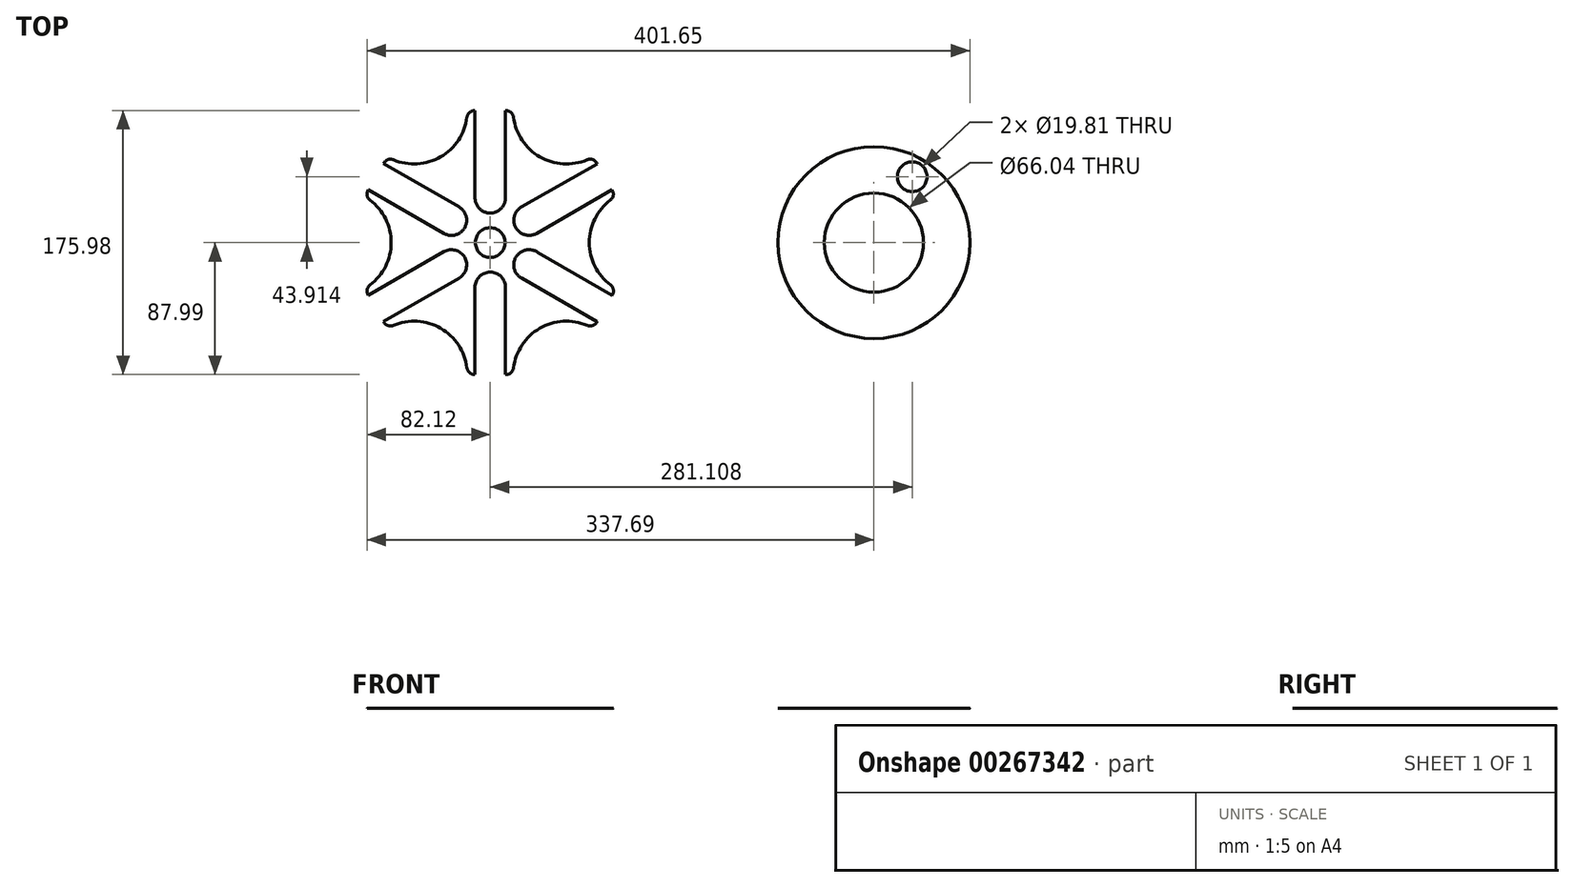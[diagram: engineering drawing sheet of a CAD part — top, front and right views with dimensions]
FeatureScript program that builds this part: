
annotation { "Feature Type Name" : "Feature", "Feature Type Description" : "" }
export const myFeature = defineFeature(function(context is Context, id is Id, definition is map)
    precondition{}
    {
        {
            var Q0;
            Q0=qCreatedBy(makeId("Top.planeOp"),FACE);
            var sketch = newSketch(context, id + "F0", { "sketchPlane" : qUnion([Q0])});
            skLineSegment(sketch, "E0", {"start": v(-17.88, 30.74) * mm, "end": v(-21.07, 36.23) * mm});
            skArc(sketch, "E1", {"start": v(-51.08, 88.15) * mm, "mid": v(-51.21, 88.23) * mm, "end": v(-51.35, 88.3) * mm});
            skLineSegment(sketch, "E2", {"start": v(-152.58, 87.67) * mm, "end": v(-152.68, 87.83) * mm});
            skArc(sketch, "E3.trimOffspring", {"start": v(-152.4, 87.99) * mm, "mid": v(-152.54, 87.9) * mm, "end": v(-152.68, 87.83) * mm});
            skArc(sketch, "E4", {"start": v(-17.78, 30.8) * mm, "mid": v(-35.56, 0) * mm, "end": v(-17.78, -30.8) * mm});
            skLineSegment(sketch, "E5", {"start": v(-17.78, -30.8) * mm, "end": v(-20.95, -36.3) * mm});
            skLineSegment(sketch, "E6", {"start": v(-86.36, -87.99) * mm, "end": v(-92.7, -87.99) * mm});
            skLineSegment(sketch, "E7", {"start": v(-170.18, -57.2) * mm, "end": v(-172.72, -52.8) * mm});
            skLineSegment(sketch, "E8.MirrorCS", {"start": v(-152.4, 87.99) * mm, "end": v(-152.58, 87.67) * mm});
            skLineSegment(sketch, "E9.MirrorCS", {"start": v(-86.36, 87.99) * mm, "end": v(-91.44, 87.99) * mm});
            skLineSegment(sketch, "E10.MirrorCS", {"start": v(-17.78, 30.8) * mm, "end": v(-20.95, 36.3) * mm});
            skArc(sketch, "E11", {"start": v(-33.02, -57.2) * mm, "mid": v(-68.58, -57.2) * mm, "end": v(-86.36, -87.99) * mm});
            skArc(sketch, "E12", {"start": v(-116.84, -87.99) * mm, "mid": v(-134.62, -57.2) * mm, "end": v(-170.18, -57.2) * mm});
            skArc(sketch, "E13", {"start": v(-185.42, -30.8) * mm, "mid": v(-167.64, 0) * mm, "end": v(-185.42, 30.8) * mm});
            skArc(sketch, "E14", {"start": v(-86.36, 87.99) * mm, "mid": v(-68.58, 57.2) * mm, "end": v(-33.02, 57.2) * mm});
            skArc(sketch, "E15", {"start": v(-170.18, 57.2) * mm, "mid": v(-134.62, 57.2) * mm, "end": v(-116.84, 87.99) * mm});
            skLineSegment(sketch, "E16.trimOffspring", {"start": v(-170.18, 57.2) * mm, "end": v(-173.35, 51.7) * mm});
            skLineSegment(sketch, "E17", {"start": v(-116.84, 87.99) * mm, "end": v(-111.76, 87.99) * mm});
            skLineSegment(sketch, "E18", {"start": v(-185.42, 30.8) * mm, "end": v(-182.25, 36.3) * mm});
            skLineSegment(sketch, "E19", {"start": v(-170.18, -57.2) * mm, "end": v(-173.35, -51.7) * mm});
            skLineSegment(sketch, "E20", {"start": v(-116.84, -87.99) * mm, "end": v(-110.5, -87.99) * mm});
            skLineSegment(sketch, "E21", {"start": v(-33.02, -57.2) * mm, "end": v(-29.85, -51.7) * mm});
            skLineSegment(sketch, "E22.trimOffspring", {"start": v(-182.25, 36.3) * mm, "end": v(-185.42, 30.8) * mm});
            skLineSegment(sketch, "E23.trimOffspring", {"start": v(-182.88, -35.2) * mm, "end": v(-185.42, -30.8) * mm});
            skLineSegment(sketch, "E24.trimOffspring", {"start": v(-29.84, 51.7) * mm, "end": v(-33.02, 57.2) * mm});
            skLineSegment(sketch, "E25.trimOffspring", {"start": v(-29.85, -51.7) * mm, "end": v(-33.02, -57.2) * mm});
            skLineSegment(sketch, "E26.trimOffspring", {"start": v(-110.5, -87.99) * mm, "end": v(-116.84, -87.99) * mm});
            skLineSegment(sketch, "E27", {"start": v(-131.93, 7.25) * mm, "end": v(-131.9, 7.22) * mm});
            skLineSegment(sketch, "E28", {"start": v(-80.13, 22.66) * mm, "end": v(-80.16, 22.64) * mm});
            skPoint(sketch, "E29.orphan", {"position": v(-68.58, 57.2) * mm});
            skPoint(sketch, "E30.orphan", {"position": v(-134.62, 57.2) * mm});
            skPoint(sketch, "E31.orphan", {"position": v(-134.62, -57.2) * mm});
            skPoint(sketch, "E32.orphan", {"position": v(-68.58, -57.2) * mm});
            skCircle(sketch, "E33.MirrorC", {"center": v(153.97, 0) * mm, "radius": 63.96 * mm});
            skCircle(sketch, "E34.MirrorC", {"center": v(153.97, 0) * mm, "radius": 33.02 * mm});
            skCircle(sketch, "E35.MirrorC", {"center": v(179.5, 43.91) * mm, "radius": 9.9 * mm});
            skPoint(sketch, "E36.orphan", {"position": v(-101.6, 79.1) * mm});
            skPoint(sketch, "E37.orphan", {"position": v(-101.6, -79.1) * mm});
            skPoint(sketch, "E38.orphan", {"position": v(-101.6, -39.55) * mm});
            skLineSegment(sketch, "E39", {"start": v(-71.33, 7.32) * mm, "end": v(-71.27, 7.25) * mm});
            skLineSegment(sketch, "E40.trimOffspring", {"start": v(-21.07, 36.23) * mm, "end": v(-20.95, 36.3) * mm});
            skCircle(sketch, "E41", {"center": v(-101.6, 0) * mm, "radius": 9.9 * mm});
            skLineSegment(sketch, "E42", {"start": v(-124.9, 19.32) * mm, "end": v(-124.98, 19.36) * mm});
            skLineSegment(sketch, "E43", {"start": v(-20.95, -36.3) * mm, "end": v(-22.86, -39.6) * mm});
            skLineSegment(sketch, "E44.trimOffspring", {"start": v(-27.94, -48.4) * mm, "end": v(-29.85, -51.7) * mm});
            skLineSegment(sketch, "E45.trimOffspring", {"start": v(-131.88, 7.25) * mm, "end": v(-131.9, 7.22) * mm});
            skPoint(sketch, "E46.trimOffspring.end.orphan", {"position": v(-80.16, 22.64) * mm});
            skPoint(sketch, "E47.start.orphan", {"position": v(-75.71, 14.95) * mm});
            skPoint(sketch, "E48.end.orphan", {"position": v(-92.7, 29.84) * mm});
            skPoint(sketch, "E49.start.orphan", {"position": v(-110.5, 29.85) * mm});
            skPoint(sketch, "E50.orphan", {"position": v(-168.39, 7.25) * mm});
            skLineSegment(sketch, "E51.trimOffspring", {"start": v(-131.88, 7.25) * mm, "end": v(-131.93, 7.25) * mm});
            skPoint(sketch, "E52.start.orphan", {"position": v(-94.85, 7.25) * mm});
            skPoint(sketch, "E53.trimOffspring.end.orphan", {"position": v(-92.7, -29.85) * mm});
            skArc(sketch, "E54", {"start": v(-111.76, 29.85) * mm, "mid": v(-101.6, 19.68) * mm, "end": v(-91.44, 29.84) * mm});
            skArc(sketch, "E55", {"start": v(-70.1, -6.48) * mm, "mid": v(-84.46, -9.68) * mm, "end": v(-80.57, -23.87) * mm});
            skArc(sketch, "E56", {"start": v(-91.44, -29.84) * mm, "mid": v(-101.6, -19.69) * mm, "end": v(-111.76, -29.85) * mm});
            skArc(sketch, "E57", {"start": v(-122.37, -23.72) * mm, "mid": v(-118.65, -9.84) * mm, "end": v(-132.53, -6.12) * mm});
            skArc(sketch, "E58", {"start": v(-132.53, 6.12) * mm, "mid": v(-118.63, 9.88) * mm, "end": v(-122.44, 23.76) * mm});
            skArc(sketch, "E59", {"start": v(-80.67, 23.81) * mm, "mid": v(-84.55, 9.93) * mm, "end": v(-70.63, 6.15) * mm});
            skLineSegment(sketch, "E60", {"start": v(-125.1, 19.16) * mm, "end": v(-124.98, 19.36) * mm});
            skLineSegment(sketch, "E61", {"start": v(-80.13, 22.66) * mm, "end": v(-80.17, 22.74) * mm});
            skLineSegment(sketch, "E62", {"start": v(-92.7, -29.85) * mm, "end": v(-83.38, -29.84) * mm});
            skLineSegment(sketch, "E63", {"start": v(-111.76, -29.85) * mm, "end": v(-119.88, -29.85) * mm});
            skLineSegment(sketch, "E64", {"start": v(-132.53, -6.12) * mm, "end": v(-184.78, -36.3) * mm});
            skLineSegment(sketch, "E65", {"start": v(-122.37, -23.72) * mm, "end": v(-175.15, -54.2) * mm});
            skLineSegment(sketch, "E66", {"start": v(-132.53, 6.12) * mm, "end": v(-182.88, 35.2) * mm});
            skLineSegment(sketch, "E67", {"start": v(-122.44, 23.76) * mm, "end": v(-173.35, 53.16) * mm});
            skLineSegment(sketch, "E68", {"start": v(-111.76, 29.85) * mm, "end": v(-111.76, 87.99) * mm});
            skLineSegment(sketch, "E69", {"start": v(-91.44, 29.84) * mm, "end": v(-91.44, 87.99) * mm});
            skLineSegment(sketch, "E70", {"start": v(-71.27, -5.8) * mm, "end": v(-7.8, -42.45) * mm});
            skLineSegment(sketch, "E71", {"start": v(-80.57, -23.87) * mm, "end": v(-13.2, -62.76) * mm});
            skLineSegment(sketch, "E72", {"start": v(-80.75, 23.77) * mm, "end": v(-80.67, 23.81) * mm});
            skLineSegment(sketch, "E73", {"start": v(-70.63, 6.15) * mm, "end": v(-12.6, 39.65) * mm});
            skLineSegment(sketch, "E74", {"start": v(-80.75, 23.77) * mm, "end": v(-18.8, 58.78) * mm});
            skLineSegment(sketch, "E75", {"start": v(-111.76, -29.85) * mm, "end": v(-111.76, -93.35) * mm});
            skLineSegment(sketch, "E76", {"start": v(-91.44, -29.84) * mm, "end": v(-91.44, -93.34) * mm});
            skPoint(sketch, "E77.trimOffspring.end.orphan", {"position": v(-92.7, 87.99) * mm});
            skPoint(sketch, "E78.orphan", {"position": v(-182.25, -36.3) * mm});
            skPoint(sketch, "E79.trimOffspring.end.orphan", {"position": v(-13.2, -56.9) * mm});
            skLineSegment(sketch, "E80.trimOffspring", {"start": v(-22.86, -39.6) * mm, "end": v(-15.66, -43.75) * mm});
            skPoint(sketch, "E81.start.orphan", {"position": v(-96.52, -29.85) * mm});
            skLineSegment(sketch, "E82.trimOffspring", {"start": v(-70.63, 6.15) * mm, "end": v(-67.08, 0) * mm});
            skLineSegment(sketch, "E83.trimOffspring", {"start": v(-80.75, 23.77) * mm, "end": v(-83.93, 29.4) * mm});
            skPoint(sketch, "E84.orphan", {"position": v(-96.52, 29.84) * mm});
            skPoint(sketch, "E85.end.orphan", {"position": v(-119.88, -28.03) * mm});
            skCircle(sketch, "E86", {"center": v(153.97, 0) * mm, "radius": 9.9 * mm});
            skSolve(sketch);
        }
        {
            var Q0;
            {var subQ4=sQuery(id+"F0.wireOp",EDGE,"E5");Q0=makeQuery(id+"F0.imprint","IMPRINT",FACE,{"disambiguationData":[TD([[makeQuery(id+"F0.imprint","IMPRINT",EDGE,{"derivedFrom":subQ4}),-1.0]])]});}
            var Q1;
            {var subQ0=sQuery(id+"F0.wireOp",EDGE,"E22.trimOffspring");Q1=makeQuery(id+"F0.imprint","IMPRINT",FACE,{"disambiguationData":[TD([[makeQuery(id+"F0.imprint","IMPRINT",EDGE,{"derivedFrom":subQ0}),1.0]])]});}
            var Q2;
            Q2=makeQuery(id+"F0.imprint","IMPRINT",FACE,{"disambiguationData":[TD([[makeQuery(id+"F0.imprint","IMPRINT",EDGE,{"derivedFrom":sQuery(id+"F0.wireOp",EDGE,"uSZaNnna-1jwC-4t9j-SezL-AJG7YBYIZrXv")}),-1.0]])]});
            var Q3;
            Q3=makeQuery(id+"F0.imprint","IMPRINT",FACE,{"disambiguationData":[TD([[makeQuery(id+"F0.imprint","IMPRINT",EDGE,{"derivedFrom":sQuery(id+"F0.wireOp",EDGE,"D1ePEbcy-xajl-UQ1t-o9PS-B0dAxn1GL7n1")}),1.0]])]});
            var Q4;
            Q4=makeQuery(id+"F0.imprint","IMPRINT",FACE,{"disambiguationData":[TD([[makeQuery(id+"F0.imprint","IMPRINT",EDGE,{"derivedFrom":sQuery(id+"F0.wireOp",EDGE,"ikVYGcS1-sRuT-H6B9-o1VI-YZQh97ZToIua")}),1.0]])]});
            var Q5;
            {var subQ6=sQuery(id+"F0.wireOp",EDGE,"dRBBgPbQ-JmLF-MllI-72Dp-3rJgf66h9gDL");Q5=makeQuery(id+"F0.imprint","IMPRINT",FACE,{"disambiguationData":[TD([[makeQuery(id+"F0.imprint","IMPRINT",EDGE,{"derivedFrom":subQ6}),-1.0]])]});}
            var Q6;
            {var subQ0=sQuery(id+"F0.wireOp",EDGE,"KPSCcwpI-83Hp-GgRb-4KHc-9A43FENirF3n");Q6=makeQuery(id+"F0.imprint","IMPRINT",FACE,{"disambiguationData":[TD([[makeQuery(id+"F0.imprint","IMPRINT",EDGE,{"derivedFrom":subQ0}),-1.0]])]});}
            var Q7;
            Q7=makeQuery(id+"F0.imprint","IMPRINT",FACE,{"disambiguationData":[TD([[makeQuery(id+"F0.imprint","IMPRINT",EDGE,{"derivedFrom":sQuery(id+"F0.wireOp",EDGE,"4uL0ZJAi-WeLn-BYnS-dUuS-PUcKbwxaNKFB")}),-1.0]])]});
            var Q8;
            Q8=makeQuery(id+"F0.imprint","IMPRINT",FACE,{"disambiguationData":[TD([[makeQuery(id+"F0.imprint","IMPRINT",EDGE,{"derivedFrom":sQuery(id+"F0.wireOp",EDGE,"Ppr8QDiS-9UEB-n1fa-jZbn-iAMovaq8OuiE")}),1.0]])]});
            var Q9;
            {var subQ4=sQuery(id+"F0.wireOp",EDGE,"8d62YASr-I1gK-Lq7n-FRaW-UgMCD8gDFPTT");Q9=makeQuery(id+"F0.imprint","IMPRINT",FACE,{"disambiguationData":[TD([[makeQuery(id+"F0.imprint","IMPRINT",EDGE,{"derivedFrom":subQ4}),1.0]])]});}
            var Q10;
            {var subQ1=sQuery(id+"F0.wireOp",EDGE,"E40.trimOffspring");var subQ7=makeQuery(id+"F0.imprint","INTERSECT",VERTEX,{"derivedFrom":[sQuery(id+"F0.wireOp",EDGE,"E0"),subQ1]});Q10=makeQuery(id+"F0.imprint","IMPRINT",FACE,{"disambiguationData":[TD([[makeQuery(id+"F0.imprint","IMPRINT",EDGE,{"disambiguationData":[TD([[subQ7,1.0]])],"derivedFrom":subQ1}),1.0]])]});}
            var Q11;
            Q11=makeQuery(id+"F0.imprint","IMPRINT",FACE,{"disambiguationData":[TD([[makeQuery(id+"F0.imprint","IMPRINT",EDGE,{"derivedFrom":sQuery(id+"F0.wireOp",EDGE,"E48")}),-1.0]])]});
            var Q12;
            Q12=makeQuery(id+"F0.imprint","IMPRINT",FACE,{"disambiguationData":[TD([[makeQuery(id+"F0.imprint","IMPRINT",EDGE,{"derivedFrom":sQuery(id+"F0.wireOp",EDGE,"wmZiJQRu-9ril-CLY3-VCLZ-qn6qzMTUEO2v")}),1.0]])]});
            var Q13;
            Q13=makeQuery(id+"F0.imprint","IMPRINT",FACE,{"disambiguationData":[TD([[makeQuery(id+"F0.imprint","IMPRINT",EDGE,{"derivedFrom":sQuery(id+"F0.wireOp",EDGE,"BJWzxmc5-WlMr-A5qr-5WOj-xHkCWyfmV3LD")}),-1.0]])]});
            var Q14;
            Q14=makeQuery(id+"F0.imprint","IMPRINT",FACE,{"disambiguationData":[TD([[makeQuery(id+"F0.imprint","IMPRINT",EDGE,{"derivedFrom":sQuery(id+"F0.wireOp",EDGE,"CQ3IfXNZ-0Cpx-K8aI-YxXh-zfcO3uTLte8J")}),1.0]])]});
            var Q15;
            Q15=makeQuery(id+"F0.imprint","IMPRINT",FACE,{"disambiguationData":[TD([[makeQuery(id+"F0.imprint","IMPRINT",EDGE,{"derivedFrom":sQuery(id+"F0.wireOp",EDGE,"WXQhSTUE-mwQW-dd3I-SJBa-6qlZWPCet8Dx")}),-1.0]])]});
            var Q16;
            Q16=makeQuery(id+"F0.imprint","IMPRINT",FACE,{"disambiguationData":[TD([[makeQuery(id+"F0.imprint","IMPRINT",EDGE,{"derivedFrom":sQuery(id+"F0.wireOp",EDGE,"TLkUIHZT-hsmt-kgMV-qJ7m-XfVgcyBmOZD1")}),1.0]])]});
            extrude(context, id + "F1", {"entities" : qUnion([Q0, Q1, Q2, Q3, Q4, Q5, Q6, Q7, Q8, Q9, Q10, Q11, Q12, Q13, Q14, Q15, Q16]), "depth" : 1 / 203.2 * mm});
        }
        {
            var Q0;
            Q0=makeQuery(id+"F1.opExtrude","SWEPT_EDGE",EDGE,{"disambiguationData":[OSD([sQuery(id+"F0.wireOp",EDGE,"E0"),sQuery(id+"F0.wireOp",EDGE,"E4")])]});
            var Q1;
            Q1=makeQuery(id+"F1.opExtrude","SWEPT_EDGE",EDGE,{"disambiguationData":[OSD([sQuery(id+"F0.wireOp",EDGE,"E4"),sQuery(id+"F0.wireOp",EDGE,"E5")])]});
            var Q2;
            Q2=makeQuery(id+"F1.opExtrude","SWEPT_EDGE",EDGE,{"disambiguationData":[OSD([sQuery(id+"F0.wireOp",EDGE,"E11"),sQuery(id+"F0.wireOp",EDGE,"E25.trimOffspring")])]});
            var Q3;
            Q3=makeQuery(id+"F1.opExtrude","SWEPT_EDGE",EDGE,{"disambiguationData":[OSD([sQuery(id+"F0.wireOp",EDGE,"E6"),sQuery(id+"F0.wireOp",EDGE,"E11")])]});
            var Q4;
            Q4=makeQuery(id+"F1.opExtrude","SWEPT_EDGE",EDGE,{"disambiguationData":[OSD([sQuery(id+"F0.wireOp",EDGE,"E12"),sQuery(id+"F0.wireOp",EDGE,"E26.trimOffspring")])]});
            var Q5;
            Q5=makeQuery(id+"F1.opExtrude","SWEPT_EDGE",EDGE,{"disambiguationData":[OSD([sQuery(id+"F0.wireOp",EDGE,"E12"),sQuery(id+"F0.wireOp",EDGE,"E19")])]});
            var Q6;
            Q6=makeQuery(id+"F1.opExtrude","SWEPT_EDGE",EDGE,{"disambiguationData":[OSD([sQuery(id+"F0.wireOp",EDGE,"E13"),sQuery(id+"F0.wireOp",EDGE,"E23.trimOffspring")])]});
            var Q7;
            Q7=makeQuery(id+"F1.opExtrude","SWEPT_EDGE",EDGE,{"disambiguationData":[OSD([sQuery(id+"F0.wireOp",EDGE,"E13"),sQuery(id+"F0.wireOp",EDGE,"E22.trimOffspring")])]});
            var Q8;
            Q8=makeQuery(id+"F1.opExtrude","SWEPT_EDGE",EDGE,{"disambiguationData":[OSD([sQuery(id+"F0.wireOp",EDGE,"E15"),sQuery(id+"F0.wireOp",EDGE,"E17")])]});
            var Q9;
            Q9=makeQuery(id+"F1.opExtrude","SWEPT_EDGE",EDGE,{"disambiguationData":[OSD([sQuery(id+"F0.wireOp",EDGE,"E9.MirrorCS"),sQuery(id+"F0.wireOp",EDGE,"E14")])]});
            var Q10;
            Q10=makeQuery(id+"F1.opExtrude","SWEPT_EDGE",EDGE,{"disambiguationData":[OSD([sQuery(id+"F0.wireOp",EDGE,"E14"),sQuery(id+"F0.wireOp",EDGE,"E24.trimOffspring")])]});
            var Q11;
            Q11=makeQuery(id+"F1.opExtrude","SWEPT_EDGE",EDGE,{"disambiguationData":[OSD([sQuery(id+"F0.wireOp",EDGE,"E15"),sQuery(id+"F0.wireOp",EDGE,"E16.trimOffspring")])]});
            fillet(context, id + "F2", {"entities" : qUnion([Q0, Q1, Q2, Q3, Q4, Q5, Q6, Q7, Q8, Q9, Q10, Q11]), "radius" : 5.08 * mm, "tangentPropagation" : true, "allowEdgeOverflow" : false});
        }
        {
            var Q0;
            Q0=makeQuery(id+"F0.imprint","IMPRINT",FACE,{"disambiguationData":[TD([[makeQuery(id+"F0.imprint","IMPRINT",EDGE,{"derivedFrom":sQuery(id+"F0.wireOp",EDGE,"E34.MirrorC")}),-1.0]])]});
            var Q1;
            Q1=makeQuery(id+"F0.imprint","IMPRINT",FACE,{"disambiguationData":[TD([[makeQuery(id+"F0.imprint","IMPRINT",EDGE,{"derivedFrom":sQuery(id+"F0.wireOp",EDGE,"E33.MirrorC")}),-1.0]])]});
            extrude(context, id + "F3", {"entities" : qUnion([Q0, Q1]), "depth" : 1 / 203.2 * mm});
        }
    });
